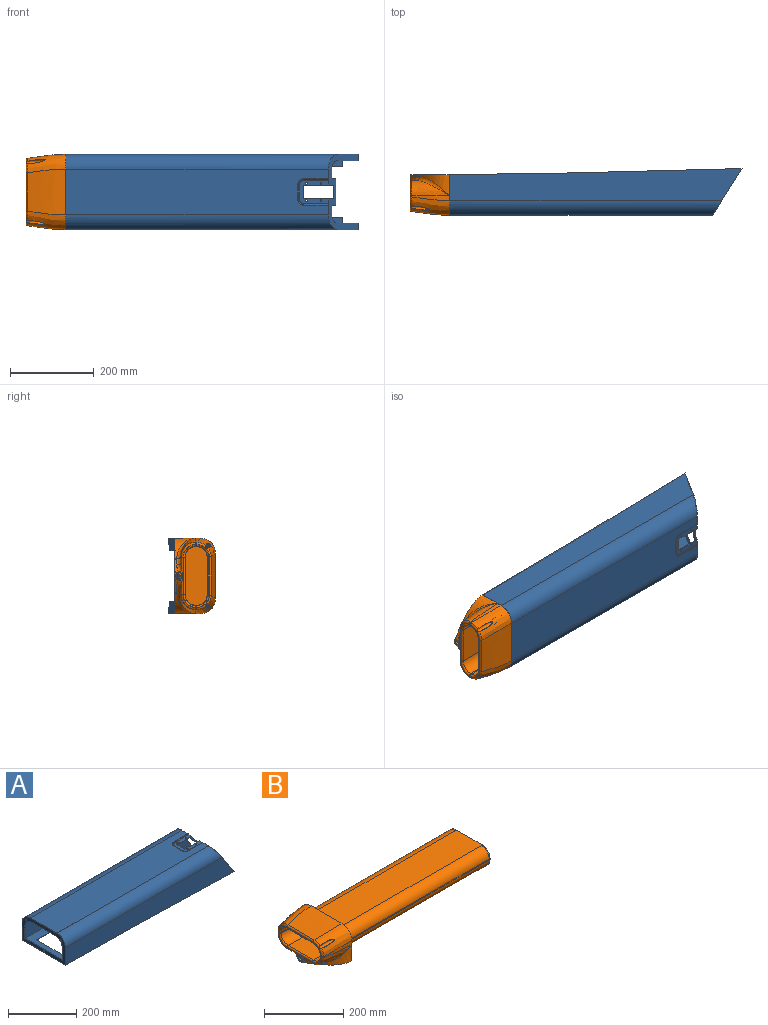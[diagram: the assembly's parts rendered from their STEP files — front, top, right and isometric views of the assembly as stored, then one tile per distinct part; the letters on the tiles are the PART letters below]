
ASSEMBLY  parts=2 mates=1
PART A: 75 faces, bbox 709.8x189.3x121.3 mm
  f0: plane 180x97.34mm, normal (-1,0,0), area 5927.6mm2, adj f2,f3,f4,f5,f6,f29,f34,f35
  f1: plane 177x94.35mm, normal (1,0,0), area 5150.5mm2, adj f2,f3,f4,f5,f6,f29,f52,f53
  f2: plane 41.34x1.5mm, normal (0,-1,0), area 62mm2, adj f0,f1,f3,f29
  f3: plane 156x1.5mm, normal (0,0,1), area 234mm2, adj f0,f1,f2,f4
  f4: plane 41.34x1.5mm, normal (0,1,0), area 62mm2, adj f0,f1,f3,f5
  f5: cylinder r=32mm len=32mm, axis (1,0,0), area 75.4mm2, adj f0,f1,f4,f6
  f6: plane 92x1.5mm, normal (0,0,-1), area 138mm2, adj f0,f1,f5,f29
  f7: plane 18.62x1.27mm, normal (0.53,0,-0.84), area 27.9mm2, adj f8,f30,f32,f50
  f8: bspline ~4.88x2.45mm, area 7.9mm2, adj f7,f9,f32,f50
  f9: plane 14.93x10.21mm, normal (0,1,0), area 25.1mm2, adj f8,f10,f32,f50
  f10: plane 63x1.27mm, normal (0.53,0,-0.84), area 94.5mm2, adj f9,f11,f32,f50
  f11: plane 14.93x10.21mm, normal (0,-1,0), area 25.1mm2, adj f10,f12,f32,f50
  f12: bspline ~4.88x2.45mm, area 7.9mm2, adj f11,f13,f32,f50
  f13: plane 18.62x1.27mm, normal (0.53,0,-0.84), area 27.9mm2, adj f12,f14,f32,f50
  f14: bspline ~23.13x20mm, area 54.8mm2, adj f13,f15,f32,f50
  f15: plane 77x50mm, normal (0,1,0), area 186.7mm2, adj f14,f16,f32,f42,f50,f60
  f16: plane 15x1.5mm, normal (1,0,-0.03), area 22.5mm2, adj f15,f17,f42,f60
  f17: plane 634.68x15.34mm, normal (0,1,0), area 951mm2, adj f16,f18,f42,f60
  f18: plane 120x1.5mm, normal (1,0,-0.01), area 180mm2, adj f17,f19,f42,f60
  f19: plane 634.68x15.34mm, normal (0,-1,0), area 951mm2, adj f18,f20,f42,f60
  f20: plane 15x1.5mm, normal (1,0,-0.03), area 22.5mm2, adj f19,f21,f42,f60
  f21: plane 77x50mm, normal (0,-1,0), area 186.7mm2, adj f20,f30,f32,f42,f50,f60
  f22: plane 72.66x18.8mm, normal (0,-1,0), area 122.6mm2, adj f23,f31,f32,f44,f50,f62
  f23: plane 33x1.5mm, normal (1,0,0), area 49.5mm2, adj f22,f24,f44,f62
  f24: plane 72.66x18.8mm, normal (0,1,0), area 122.6mm2, adj f23,f31,f32,f44,f50,f62
  f25: cylinder r=2.1mm len=4.2mm, axis (0,0,-1), area 19.8mm2, adj f44,f62
  f26: cylinder r=2.1mm len=4.2mm, axis (0,0,-1), area 19.8mm2, adj f44,f62
  f27: cylinder r=2.1mm len=4.2mm, axis (0,0,1), area 19.8mm2, adj f44,f62
  f28: cylinder r=2.1mm len=4.2mm, axis (0,0,1), area 19.8mm2, adj f44,f62
  f29: cylinder r=32mm len=32mm, axis (1,0,0), area 75.4mm2, adj f0,f1,f2,f6
  f30: bspline ~23.13x20mm, area 54.8mm2, adj f7,f21,f32,f50
  f31: plane 33x1.27mm, normal (-0.53,0,0.84), area 49.5mm2, adj f22,f24,f32,f50
  f32: plane 189.32x121.32mm, normal (0.84,0,0.53), area 6177.9mm2, adj f7,f8,f9,f10,f11,f12,f13,f14
  f33: torus R=10mm, axis (0,0,-1), area 36mm2, adj f38,f40,f44,f47
  f34: cylinder r=35mm len=651.27mm, axis (-1,0,0), area 35196.3mm2, adj f0,f32,f35,f43
  f35: plane 700.52x77mm, normal (0,1,0), area 46012.1mm2, adj f0,f32,f34,f42
  f36: cylinder r=35mm len=651.27mm, axis (-1,0,0), area 35196.3mm2, adj f0,f32,f43,f45
  f37: cylinder r=2mm len=60.82mm, axis (1,0,0), area 126.7mm2, adj f32,f39,f44,f49
  f38: torus R=13.46mm, axis (0,0,1), area 41.2mm2, adj f33,f41,f43,f48
  f39: cylinder r=2mm len=60.18mm, axis (1,0,0), area 125.4mm2, adj f32,f37,f43,f46
  f40: cylinder r=2mm len=60.82mm, axis (1,0,0), area 126.7mm2, adj f32,f33,f41,f44
  f41: cylinder r=2mm len=60.18mm, axis (1,0,0), area 125.4mm2, adj f32,f38,f40,f43
  f42: extruded ~700x180mm, area 44397.4mm2, adj f0,f15,f16,f17,f18,f19,f20,f21
  f43: plane 629.11x110mm, normal (0,0,1), area 64714.9mm2, adj f0,f32,f34,f36,f38,f39,f41,f46
  f44: plane 70.82x55.6mm, normal (0,0,1), area 1817.2mm2, adj f22,f23,f24,f25,f26,f27,f28,f32
  f45: plane 700.52x77mm, normal (0,-1,0), area 46012.1mm2, adj f0,f32,f36,f42
  f46: torus R=13.46mm, axis (0,0,1), area 41.2mm2, adj f39,f43,f48,f49
  f47: cylinder r=2mm len=35.6mm, axis (0,-1,0), area 74.6mm2, adj f33,f44,f48,f49
  f48: cylinder r=2mm len=35.6mm, axis (0,-1,0), area 74.6mm2, adj f38,f43,f46,f47
  f49: torus R=10mm, axis (0,0,-1), area 36mm2, adj f37,f44,f46,f47
  f50: plane 185.92x117.84mm, normal (-0.84,0,-0.53), area 5635.5mm2, adj f7,f8,f9,f10,f11,f12,f13,f14
  f51: torus R=10mm, axis (0,0,-1), area 67.2mm2, adj f56,f58,f62,f65
  f52: cylinder r=33.5mm len=647.99mm, axis (-1,0,0), area 33540.5mm2, adj f1,f50,f53,f61
  f53: plane 700.83x80.52mm, normal (0,-1,0), area 44601.5mm2, adj f1,f50,f52,f60
  f54: cylinder r=33.5mm len=647.99mm, axis (-1,0,0), area 33540.5mm2, adj f1,f50,f61,f63
  f55: cylinder r=3.5mm len=59.99mm, axis (1,0,0), area 217.8mm2, adj f50,f57,f62,f67
  f56: torus R=13.46mm, axis (0,0,1), area 10.9mm2, adj f51,f59,f61,f66
  f57: cylinder r=0.5mm len=58.88mm, axis (1,0,0), area 30.8mm2, adj f50,f55,f61,f64
  f58: cylinder r=3.5mm len=59.99mm, axis (1,0,0), area 217.8mm2, adj f50,f51,f59,f62
  f59: cylinder r=0.5mm len=58.88mm, axis (1,0,0), area 30.8mm2, adj f50,f56,f58,f61
  f60: bspline ~695.73x177mm, area 41958.3mm2, adj f1,f15,f16,f17,f18,f19,f20,f21
  f61: plane 626.79x110mm, normal (0,0,-1), area 64510.7mm2, adj f1,f50,f52,f54,f56,f57,f59,f64
  f62: plane 69.99x55.6mm, normal (0,0,-1), area 1798.6mm2, adj f22,f23,f24,f25,f26,f27,f28,f50
  f63: plane 700.83x80.52mm, normal (0,1,0), area 44769.7mm2, adj f1,f50,f54,f60
  f64: torus R=13.46mm, axis (0,0,1), area 10.9mm2, adj f57,f61,f66,f67
  f65: cylinder r=3.5mm len=35.6mm, axis (0,-1,0), area 130.5mm2, adj f51,f62,f66,f67
  f66: cylinder r=0.5mm len=35.6mm, axis (0,-1,0), area 18.6mm2, adj f56,f61,f64,f65
  f67: torus R=10mm, axis (0,0,-1), area 67.2mm2, adj f55,f62,f64,f65
  f68: cylinder r=3.2mm len=6.42mm, axis (0.01,0,1), area 30.2mm2, adj f42,f60
  f69: cylinder r=3.2mm len=6.44mm, axis (0.03,0,1), area 30.2mm2, adj f42,f60
  f70: cylinder r=3.2mm len=6.42mm, axis (0.01,0,1), area 30.2mm2, adj f42,f60
  f71: cylinder r=3.2mm len=6.44mm, axis (0.03,0,1), area 30.2mm2, adj f42,f60
  f72: cylinder r=2.65mm len=5.3mm, axis (-1,0,0), area 25mm2, adj f0,f1
  f73: cylinder r=2.65mm len=5.3mm, axis (-1,0,0), area 25mm2, adj f0,f1
  f74: cylinder r=2.65mm len=5.3mm, axis (-1,0,0), area 25mm2, adj f0,f1
PART B: 178 faces, bbox 641.3x217.8x135.3 mm
  f0: bspline ~5.71x5.71mm, area 5.6mm2, adj f1,f60,f152
  f1: bspline ~42.02x10.59mm, area 83.3mm2, adj f0,f60,f155
  f2: bspline ~5.71x5.71mm, area 5.6mm2, adj f3,f57,f136
  f3: bspline ~42.02x10.59mm, area 83.3mm2, adj f2,f57,f138
  f4: torus R=5.25mm, axis (-1,0,0), area 1.1mm2, adj f5,f6,f54,f159
  f5: bspline ~10.4x4.74mm, area 12.4mm2, adj f4,f7,f54,f130
  f6: bspline ~10.4x4.74mm, area 12.4mm2, adj f4,f7,f54,f145
  f7: torus R=5.25mm, axis (-1,0,0), area 1.1mm2, adj f5,f6,f54,f174
  f8: torus R=10mm, axis (1,0,0), area 158.2mm2, adj f63,f164,f165,f173
  f9: bspline ~6.32x5.84mm, area 27.3mm2, adj f10,f63,f101,f164
  f10: bspline ~6.3x5.71mm, area 30.2mm2, adj f9,f11,f63,f96
  f11: bspline ~7.14x6.27mm, area 29mm2, adj f10,f12,f63,f95
  f12: bspline ~3.15x3.13mm, area 7.5mm2, adj f11,f13,f63,f99
  f13: torus R=10mm, axis (-1,0,0), area 5.6mm2, adj f12,f14,f63,f166
  f14: bspline ~3.15x3.13mm, area 7.5mm2, adj f13,f15,f63,f86
  f15: bspline ~7.14x6.27mm, area 29mm2, adj f14,f16,f63,f82
  f16: bspline ~6.3x5.71mm, area 30.2mm2, adj f15,f17,f63,f83
  f17: bspline ~6.32x5.84mm, area 27.3mm2, adj f16,f63,f88,f165
  f18: plane 147.46x58.73mm, normal (1,0,0), area 7994.1mm2, adj f19,f20,f21,f22,f41,f43,f45,f47
  f19: extruded ~28.37x28mm, area 132.8mm2, adj f18,f43,f44,f45
  f20: extruded ~27.63x27.63mm, area 130.4mm2, adj f18,f41,f42,f43
  f21: extruded ~27.63x27.63mm, area 130.4mm2, adj f18,f40,f41,f47
  f22: extruded ~28.37x28mm, area 132.8mm2, adj f18,f45,f46,f47
  f23: plane 141.46x52.73mm, normal (-1,0,0), area 6928.6mm2, adj f50,f51,f52,f53,f120,f122,f123,f124
  f24: bspline ~31.63x31.63mm, area 287.4mm2, adj f25,f26,f65,f79,f173
  f25: cylinder r=4mm len=4mm, axis (0,0,-1), area 19.5mm2, adj f24,f27,f80,f173
  f26: cylinder r=4mm len=92.19mm, axis (0,-1,0), area 579.3mm2, adj f24,f28,f78,f173
  f27: bspline ~32.37x32mm, area 292.5mm2, adj f25,f29,f81,f173
  f28: bspline ~31.63x31.63mm, area 287.4mm2, adj f26,f30,f64,f77,f173
  f29: cylinder r=4mm len=90.71mm, axis (0,-1,0), area 570mm2, adj f27,f31,f74,f173
  f30: cylinder r=4mm len=4mm, axis (0,0,1), area 19.5mm2, adj f28,f31,f76,f173
  f31: bspline ~32.37x32mm, area 292.5mm2, adj f29,f30,f75,f173
  f32: bspline ~31.63x31.63mm, area 287.4mm2, adj f33,f34,f42,f175
  f33: cylinder r=4mm len=92.19mm, axis (0,1,0), area 579.3mm2, adj f32,f35,f41,f175
  f34: cylinder r=4mm len=4mm, axis (0,0,1), area 19.5mm2, adj f32,f36,f43,f175
  f35: bspline ~31.63x31.63mm, area 287.4mm2, adj f33,f37,f40,f175
  f36: bspline ~32.37x32mm, area 292.5mm2, adj f34,f38,f44,f175
  f37: cylinder r=4mm len=4mm, axis (0,0,-1), area 19.5mm2, adj f35,f39,f47,f175
  f38: cylinder r=4mm len=90.71mm, axis (0,-1,0), area 570mm2, adj f36,f39,f45,f175
  f39: bspline ~32.37x32mm, area 292.5mm2, adj f37,f38,f46,f175
  f40: bspline ~501x27.63mm, area 21770.7mm2, adj f21,f35,f41,f47
  f41: plane 504x92.19mm, normal (0,0,1), area 46465.4mm2, adj f18,f20,f21,f33,f40,f42
  f42: bspline ~501x27.63mm, area 21770.9mm2, adj f20,f32,f41,f43
  f43: plane 504x3.1mm, normal (0,-1,0), area 1560.7mm2, adj f18,f19,f20,f34,f42,f44
  f44: bspline ~501x28.37mm, area 22182.2mm2, adj f19,f36,f43,f45
  f45: plane 504x90.71mm, normal (0,0,-1), area 45718.5mm2, adj f18,f19,f22,f38,f44,f46
  f46: bspline ~501x28.37mm, area 22182mm2, adj f22,f39,f45,f47
  f47: plane 504x3.1mm, normal (0,1,0), area 1560.7mm2, adj f18,f21,f22,f37,f40,f46
  f48: plane 11.24x9.24mm, normal (-1,0,0), area 0mm2, adj f52,f177
  f49: plane 47.24x39.64mm, normal (1,0,0), area 0mm2, adj f52,f177
  f50: extruded ~507x25.37mm, area 20051mm2, adj f23,f120,f121,f122
  f51: extruded ~507x24.63mm, area 19633.7mm2, adj f23,f122,f123,f176
  f52: extruded ~507x24.63mm, area 19633.7mm2, adj f23,f48,f49,f123,f124,f177
  f53: extruded ~507x25.37mm, area 20050.9mm2, adj f23,f120,f124,f125
  f54: cylinder r=4.75mm len=84.5mm, axis (1,0,0), area 2512.1mm2, adj f4,f5,f6,f7,f55
  f55: plane 9.5x9.5mm, normal (-1,0,0), area 48.8mm2, adj f54,f56
  f56: cylinder r=2.65mm len=10mm, axis (1,0,0), area 166.5mm2, adj f55,f175
  f57: cylinder r=4.75mm len=83.83mm, axis (1,0,0), area 1892.6mm2, adj f2,f3,f58
  f58: plane 9.5x9.5mm, normal (-1,0,0), area 48.8mm2, adj f57,f59
  f59: cylinder r=2.65mm len=10mm, axis (1,0,0), area 166.5mm2, adj f58,f175
  f60: cylinder r=4.75mm len=83.83mm, axis (1,0,0), area 1892.4mm2, adj f0,f1,f61
  f61: plane 9.5x9.5mm, normal (-1,0,0), area 48.8mm2, adj f60,f62
  f62: cylinder r=2.65mm len=10mm, axis (1,0,0), area 166.5mm2, adj f61,f175
  f63: cylinder r=7mm len=83mm, axis (-1,0,0), area 3459.8mm2, adj f8,f9,f10,f11,f12,f13,f14,f15
  f64: cylinder r=7mm len=88.9mm, axis (-1,0,0), area 2421.1mm2, adj f28,f162,f163,f173
  f65: cylinder r=7mm len=88.9mm, axis (-1,0,0), area 2411.4mm2, adj f24,f160,f161,f173
  f66: bspline ~29.37x29mm, area 70.4mm2, adj f67,f68,f75,f166
  f67: cylinder r=1mm len=3.1mm, axis (0,0,1), area 4.9mm2, adj f66,f69,f76,f166
  f68: cylinder r=1mm len=90.71mm, axis (0,1,0), area 142.5mm2, adj f66,f70,f74,f166
  f69: bspline ~28.63x28.63mm, area 69.2mm2, adj f67,f71,f77,f166
  f70: bspline ~29.37x29mm, area 70.4mm2, adj f68,f72,f81,f166
  f71: cylinder r=1mm len=92.19mm, axis (0,-1,0), area 144.8mm2, adj f69,f73,f78,f166
  f72: cylinder r=1mm len=3.1mm, axis (0,0,-1), area 4.9mm2, adj f70,f73,f80,f166
  f73: bspline ~28.63x28.63mm, area 69.2mm2, adj f71,f72,f79,f166
  f74: plane 90.71x84mm, normal (0,0,-1), area 7619.8mm2, adj f29,f68,f75,f81
  f75: bspline ~84x28.37mm, area 3719.1mm2, adj f31,f66,f74,f76
  f76: plane 84x3.1mm, normal (0,1,0), area 260.1mm2, adj f30,f67,f75,f77
  f77: bspline ~84x27.63mm, area 3650.2mm2, adj f28,f69,f76,f78
  f78: plane 92.19x84mm, normal (0,0,1), area 7744.2mm2, adj f26,f71,f77,f79
  f79: bspline ~84x27.63mm, area 3650.2mm2, adj f24,f73,f78,f80
  f80: plane 84x3.1mm, normal (0,-1,0), area 260.1mm2, adj f25,f72,f79,f81
  f81: bspline ~84x28.37mm, area 3719.1mm2, adj f27,f70,f74,f80
  f82: bspline ~13.15x9.91mm, area 51.9mm2, adj f15,f83,f86,f89
  f83: bspline ~24.72x13.68mm, area 280.4mm2, adj f16,f82,f84,f88,f89
  f84: bspline ~22.29x20.89mm, area 367.8mm2, adj f83,f85,f88,f93
  f85: bspline ~75.02x47.4mm, area 1060.1mm2, adj f84,f87,f88,f92
  f86: cylinder r=12mm len=3.26mm, axis (0,0,1), area 3.1mm2, adj f14,f82,f166
  f87: plane 4.99x0.56mm, normal (0,0,-1), area 0.3mm2, adj f85,f88,f92,f173
  f88: bspline ~85.34x76.86mm, area 1468.2mm2, adj f17,f83,f84,f85,f87,f165,f173
  f89: cylinder r=2mm len=44.62mm, axis (0,1,0), area 93.2mm2, adj f82,f83,f90,f93,f166
  f90: bspline ~32.35x32mm, area 145.2mm2, adj f89,f91,f92,f166
  f91: cylinder r=2mm len=3.1mm, axis (0,0,1), area 8.8mm2, adj f90,f94,f163,f166
  f92: bspline ~92.32x41.63mm, area 2502.3mm2, adj f85,f87,f90,f93,f94,f173
  f93: plane 15.22x10.31mm, normal (0,0,1), area 68.8mm2, adj f84,f89,f92
  f94: bspline ~87.31x12.06mm, area 757.8mm2, adj f91,f92,f162,f173
  f95: bspline ~13.15x9.91mm, area 51.9mm2, adj f11,f96,f99,f102
  f96: bspline ~24.72x13.68mm, area 280.4mm2, adj f10,f95,f97,f101,f102
  f97: bspline ~22.29x20.89mm, area 367.8mm2, adj f96,f98,f101,f108
  f98: bspline ~75.02x47.4mm, area 1060.1mm2, adj f97,f100,f101,f106
  f99: cylinder r=12mm len=3.26mm, axis (0,0,1), area 3.1mm2, adj f12,f95,f166
  f100: plane 4.99x0.56mm, normal (0,0,-1), area 0.3mm2, adj f98,f101,f106,f173
  f101: bspline ~85.34x76.86mm, area 1468.2mm2, adj f9,f96,f97,f98,f100,f164,f173
  f102: cylinder r=2mm len=44.62mm, axis (0,-1,0), area 93.2mm2, adj f95,f96,f103,f108,f166
  f103: bspline ~32.35x32mm, area 145.2mm2, adj f102,f104,f106,f166
  f104: cylinder r=2mm len=3.1mm, axis (0,0,1), area 8.8mm2, adj f103,f109,f161,f166
  f105: cylinder r=2mm len=92.19mm, axis (0,1,0), area 260.7mm2, adj f107,f161,f163,f166
  f106: bspline ~92.32x41.63mm, area 2502.3mm2, adj f98,f100,f103,f108,f109,f173
  f107: bspline ~111.29x87.31mm, area 8882mm2, adj f105,f160,f162,f173
  f108: plane 15.22x10.31mm, normal (0,0,1), area 68.8mm2, adj f97,f102,f106
  f109: bspline ~87.31x12.06mm, area 757.8mm2, adj f104,f106,f160,f173
  f110: cylinder r=5mm len=2.63mm, axis (0,0,-1), area 1mm2, adj f63,f148,f169,f170
  f111: cylinder r=5mm len=2.63mm, axis (0,0,-1), area 1mm2, adj f63,f148,f171,f172
  f112: bspline ~29.37x29mm, area 262.9mm2, adj f113,f114,f121,f159
  f113: cylinder r=4mm len=4mm, axis (0,0,1), area 19.5mm2, adj f112,f115,f122,f159
  f114: cylinder r=4mm len=90.71mm, axis (0,1,0), area 570mm2, adj f112,f116,f120,f159
  f115: bspline ~28.63x28.63mm, area 257.8mm2, adj f113,f117,f159,f176
  f116: bspline ~29.37x29mm, area 262.9mm2, adj f114,f118,f125,f159
  f117: cylinder r=4mm len=92.19mm, axis (0,-1,0), area 579.3mm2, adj f115,f119,f123,f159
  f118: cylinder r=4mm len=4mm, axis (0,0,-1), area 19.5mm2, adj f116,f119,f124,f159
  f119: bspline ~28.63x28.63mm, area 257.8mm2, adj f117,f118,f159,f177
  f120: plane 596x90.71mm, normal (0,0,1), area 54064mm2, adj f23,f50,f53,f114,f121,f125
  f121: bspline ~91x25.37mm, area 3531mm2, adj f50,f112,f120,f122
  f122: plane 596x3.1mm, normal (0,-1,0), area 1845.6mm2, adj f23,f50,f51,f113,f121,f176
  f123: plane 596x92.19mm, normal (0,0,-1), area 54947.1mm2, adj f23,f51,f52,f117,f176,f177
  f124: plane 596x3.1mm, normal (0,1,0), area 1845.6mm2, adj f23,f52,f53,f118,f125,f177
  f125: bspline ~91x25.37mm, area 3531mm2, adj f53,f116,f120,f124
  f126: bspline ~13.15x9.91mm, area 35.3mm2, adj f127,f130,f133
  f127: bspline ~23.14x12.14mm, area 234.3mm2, adj f126,f128,f132,f133
  f128: bspline ~20.66x18.45mm, area 284.2mm2, adj f127,f129,f132,f139
  f129: bspline ~78.92x48.82mm, area 845.8mm2, adj f128,f132,f137
  f130: cylinder r=15mm len=20mm, axis (0,0,1), area 87.8mm2, adj f5,f126,f132,f148,f159,f174
  f131: plane 1.24x0.02mm, normal (0,0,1), area 0mm2, adj f132,f137,f175
  f132: extruded ~92.76x81.37mm, area 2088.6mm2, adj f127,f128,f129,f130,f131,f148,f175
  f133: cylinder r=5mm len=44.62mm, axis (0,1,0), area 232.9mm2, adj f126,f127,f134,f139,f159
  f134: bspline ~35.31x35mm, area 384.2mm2, adj f133,f135,f137,f159
  f135: cylinder r=5mm len=4.94mm, axis (0,0,1), area 21.9mm2, adj f134,f136,f140,f159
  f136: bspline ~34.57x34.57mm, area 327.2mm2, adj f2,f135,f138,f153,f159
  f137: bspline ~95.47x44.65mm, area 2610.8mm2, adj f129,f131,f134,f139,f140,f175
  f138: bspline ~92.85x43.9mm, area 4652.9mm2, adj f3,f136,f140,f156,f175
  f139: plane 15.22x10.31mm, normal (0,0,-1), area 68.8mm2, adj f128,f133,f137
  f140: extruded ~90.78x12mm, area 798.4mm2, adj f135,f137,f138,f175
  f141: bspline ~13.15x9.91mm, area 35.4mm2, adj f142,f145,f149
  f142: bspline ~23.14x12.14mm, area 234.3mm2, adj f141,f143,f147,f149
  f143: bspline ~20.66x18.45mm, area 284.2mm2, adj f142,f144,f147,f157
  f144: bspline ~78.92x48.82mm, area 845.8mm2, adj f143,f147,f154
  f145: cylinder r=15mm len=20mm, axis (0,0,1), area 87.8mm2, adj f6,f141,f147,f148,f159,f174
  f146: plane 1.24x0.02mm, normal (0,0,1), area 0mm2, adj f147,f154,f175
  f147: extruded ~92.76x81.37mm, area 2088.6mm2, adj f142,f143,f144,f145,f146,f148,f175
  f148: plane 180.02x95.02mm, normal (0,0,-1), area 4200.6mm2, adj f110,f111,f130,f132,f145,f147,f167,f168
  f149: cylinder r=5mm len=44.62mm, axis (0,-1,0), area 232.9mm2, adj f141,f142,f150,f157,f159
  f150: bspline ~35.31x35mm, area 384.2mm2, adj f149,f151,f154,f159
  f151: cylinder r=5mm len=4.94mm, axis (0,0,1), area 21.9mm2, adj f150,f152,f158,f159
  f152: bspline ~34.57x34.57mm, area 327.2mm2, adj f0,f151,f153,f155,f159
  f153: cylinder r=5mm len=92.19mm, axis (0,1,0), area 651.8mm2, adj f136,f152,f156,f159
  f154: bspline ~95.47x44.65mm, area 2610.7mm2, adj f144,f146,f150,f157,f158,f175
  f155: bspline ~92.85x43.9mm, area 4652.9mm2, adj f1,f152,f156,f158,f175
  f156: extruded ~110x90.78mm, area 9235.2mm2, adj f138,f153,f155,f175
  f157: plane 15.22x10.31mm, normal (0,0,-1), area 68.8mm2, adj f143,f149,f154
  f158: extruded ~90.78x12mm, area 798.4mm2, adj f151,f154,f155,f175
  f159: plane 151.5x70.58mm, normal (-1,0,0), area 385.4mm2, adj f4,f112,f113,f114,f115,f116,f117,f118
  f160: bspline ~93.25x40.97mm, area 3516.3mm2, adj f65,f107,f109,f161,f173
  f161: bspline ~31.61x31.61mm, area 121.3mm2, adj f65,f104,f105,f160,f166
  f162: bspline ~89.33x40.91mm, area 3556.7mm2, adj f64,f94,f107,f163,f173
  f163: bspline ~31.61x31.61mm, area 121.3mm2, adj f64,f91,f105,f162,f166
  f164: plane 86.93x82.55mm, normal (0,0,1), area 1339.7mm2, adj f8,f9,f63,f101,f167,f172,f173
  f165: plane 86.94x82.56mm, normal (0,0,1), area 1339.3mm2, adj f8,f17,f63,f88,f168,f169,f173
  f166: plane 151.5x65.8mm, normal (1,0,0), area 378.4mm2, adj f13,f66,f67,f68,f69,f70,f71,f72
  f167: plane 79x3mm, normal (-1,0,0), area 224.9mm2, adj f63,f148,f164,f172
  f168: plane 79x3mm, normal (-1,0,0), area 224.9mm2, adj f63,f148,f165,f169
  f169: bspline ~75.63x74.25mm, area 323.4mm2, adj f63,f110,f148,f165,f168
  f170: plane 0.74x0.04mm, normal (1,0,0), area 0mm2, adj f63,f110,f148
  f171: plane 0.74x0.04mm, normal (1,0,0), area 0mm2, adj f63,f111,f148
  f172: bspline ~75.63x74.25mm, area 323.4mm2, adj f63,f111,f148,f164,f167
  f173: plane 174.02x91.03mm, normal (-1,0,0), area 5352.9mm2, adj f8,f24,f25,f26,f27,f28,f29,f30
  f174: plane 1.8x1.48mm, normal (-1,0,0), area 2.6mm2, adj f7,f130,f145,f148
  f175: plane 181.12x98.12mm, normal (1,0,0), area 7365.6mm2, adj f32,f33,f34,f35,f36,f37,f38,f39
  f176: bspline ~91x24.63mm, area 3457.7mm2, adj f51,f115,f122,f123
  f177: bspline ~91x24.63mm, area 3457.7mm2, adj f48,f49,f52,f119,f123,f124
PLACE A rot(axis=(1,0,0),90deg) t=(-48,673.18,847.14)mm
PLACE B rot(axis=(1,0,0),90deg) t=(-48,673.51,847.14)mm
MATE fastened A.f0 <-> B.f175  axis (-1,0,0) through (927,-277.49,757.14)mm
